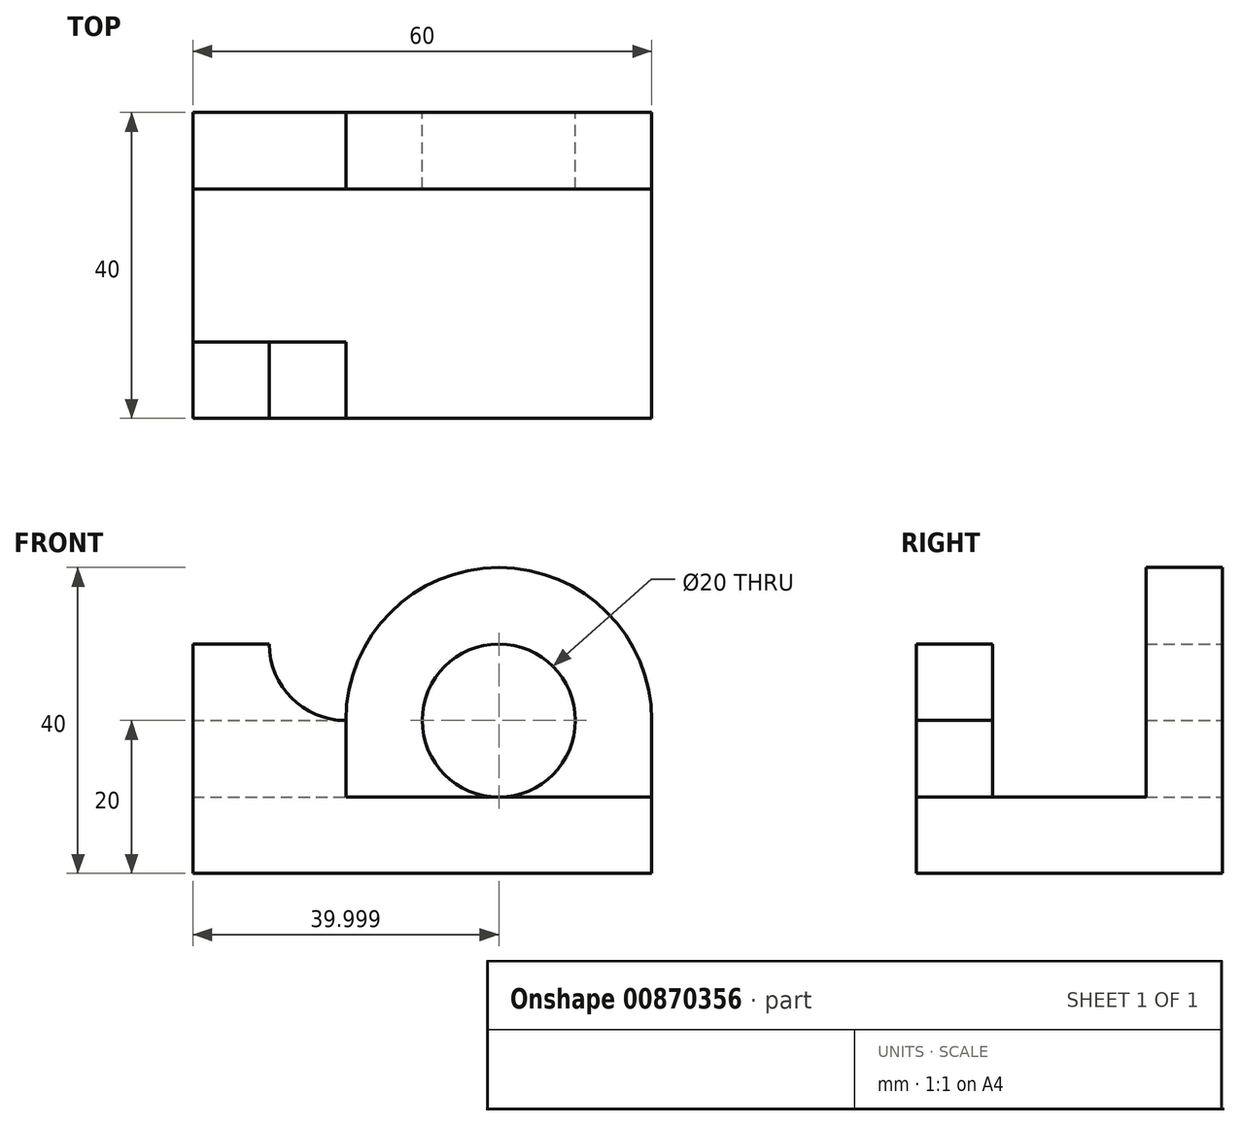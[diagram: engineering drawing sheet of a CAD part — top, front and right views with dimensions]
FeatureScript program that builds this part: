
annotation { "Feature Type Name" : "Feature", "Feature Type Description" : "" }
export const myFeature = defineFeature(function(context is Context, id is Id, definition is map)
    precondition{}
    {
        {
            var Q0;
            Q0=qCreatedBy(makeId("Front.planeOp"),FACE);
            var sketch = newSketch(context, id + "F0", { "sketchPlane" : qUnion([Q0])});
            skLineSegment(sketch, "E0.bottom", {"start": v(-24.32, 0) * mm, "end": v(35.68, 0) * mm});
            skLineSegment(sketch, "E0.left", {"start": v(-24.32, 0) * mm, "end": v(-24.32, 10) * mm});
            skLineSegment(sketch, "E0.right", {"start": v(35.68, 0) * mm, "end": v(35.68, 10) * mm});
            skCircle(sketch, "E1", {"center": v(15.68, 20) * mm, "radius": 10 * mm});
            skArc(sketch, "E2", {"start": v(35.68, 20) * mm, "mid": v(15.68, 40) * mm, "end": v(-4.32, 20) * mm});
            skLineSegment(sketch, "E3", {"start": v(35.68, 10) * mm, "end": v(35.68, 20) * mm});
            skLineSegment(sketch, "E4", {"start": v(-24.32, 10) * mm, "end": v(-24.32, 20) * mm});
            skLineSegment(sketch, "E5", {"start": v(-24.32, 20) * mm, "end": v(-4.32, 20) * mm});
            skSolve(sketch);
        }
        {
            var Q0;
            Q0 = qSketchRegion(id + "F0", true);
            extrude(context, id + "F1", {"entities" : qUnion([Q0]), "depth" : 10 * mm, "offsetDistance" : 25 * mm});
        }
        {
            var Q0;
            Q0=qCreatedBy(makeId("Top.planeOp"),FACE);
            var sketch = newSketch(context, id + "F2", { "sketchPlane" : qUnion([Q0])});
            skLineSegment(sketch, "E6.bottom", {"start": v(-24.32, 0) * mm, "end": v(35.68, 0) * mm});
            skLineSegment(sketch, "E6.top", {"start": v(-24.32, -40) * mm, "end": v(35.68, -40) * mm});
            skLineSegment(sketch, "E6.left", {"start": v(-24.32, 0) * mm, "end": v(-24.32, -40) * mm});
            skLineSegment(sketch, "E6.right", {"start": v(35.68, 0) * mm, "end": v(35.68, -40) * mm});
            skSolve(sketch);
        }
        {
            var Q0;
            Q0 = qSketchRegion(id + "F2", true);
            extrude(context, id + "F3", {"entities" : qUnion([Q0]), "operationType" : NewBodyOperationType.ADD, "depth" : 10 * mm, "offsetDistance" : 25 * mm});
        }
        {
            var Q0;
            Q0=makeQuery(id+"F3.opExtrude","CAP_FACE",FACE,{"disambiguationData":[OSD([sQuery(id+"F2.wireOp",EDGE,"E6.bottom"),sQuery(id+"F2.wireOp",EDGE,"E6.top"),sQuery(id+"F2.wireOp",EDGE,"E6.left"),sQuery(id+"F2.wireOp",EDGE,"E6.right")])],"isStart":false});
            var sketch = newSketch(context, id + "F4", { "sketchPlane" : qUnion([Q0])});
            skLineSegment(sketch, "E7.bottom", {"start": v(-24.32, -40) * mm, "end": v(-4.32, -40) * mm});
            skLineSegment(sketch, "E7.top", {"start": v(-24.32, -30) * mm, "end": v(-4.32, -30) * mm});
            skLineSegment(sketch, "E7.left", {"start": v(-24.32, -40) * mm, "end": v(-24.32, -30) * mm});
            skLineSegment(sketch, "E7.right", {"start": v(-4.32, -40) * mm, "end": v(-4.32, -30) * mm});
            skSolve(sketch);
        }
        {
            var Q0;
            Q0 = qSketchRegion(id + "F4", true);
            extrude(context, id + "F5", {"entities" : qUnion([Q0]), "operationType" : NewBodyOperationType.ADD, "depth" : 20 * mm, "offsetDistance" : 25 * mm});
        }
        {
            var Q0;
            Q0=makeQuery(id+"F5.boolean.opBoolean","MERGE",FACE,{"derivedFrom":[makeQuery(id+"F3.opExtrude","SWEPT_FACE",FACE,{"disambiguationData":[OSD([sQuery(id+"F2.wireOp",EDGE,"E6.top")])]}),makeQuery(id+"F5.opExtrude","SWEPT_FACE",FACE,{"disambiguationData":[OSD([sQuery(id+"F4.wireOp",EDGE,"E7.bottom")])]})]});
            var sketch = newSketch(context, id + "F6", { "sketchPlane" : qUnion([Q0])});
            skCircle(sketch, "E8", {"center": v(-4.32, 30) * mm, "radius": 10 * mm});
            skSolve(sketch);
        }
        {
            var Q0;
            Q0 = qSketchRegion(id + "F6", true);
            extrude(context, id + "F7", {"entities" : qUnion([Q0]), "operationType" : NewBodyOperationType.REMOVE, "oppositeDirection" : true, "depth" : 10 * mm, "offsetDistance" : 25 * mm});
        }
    });
